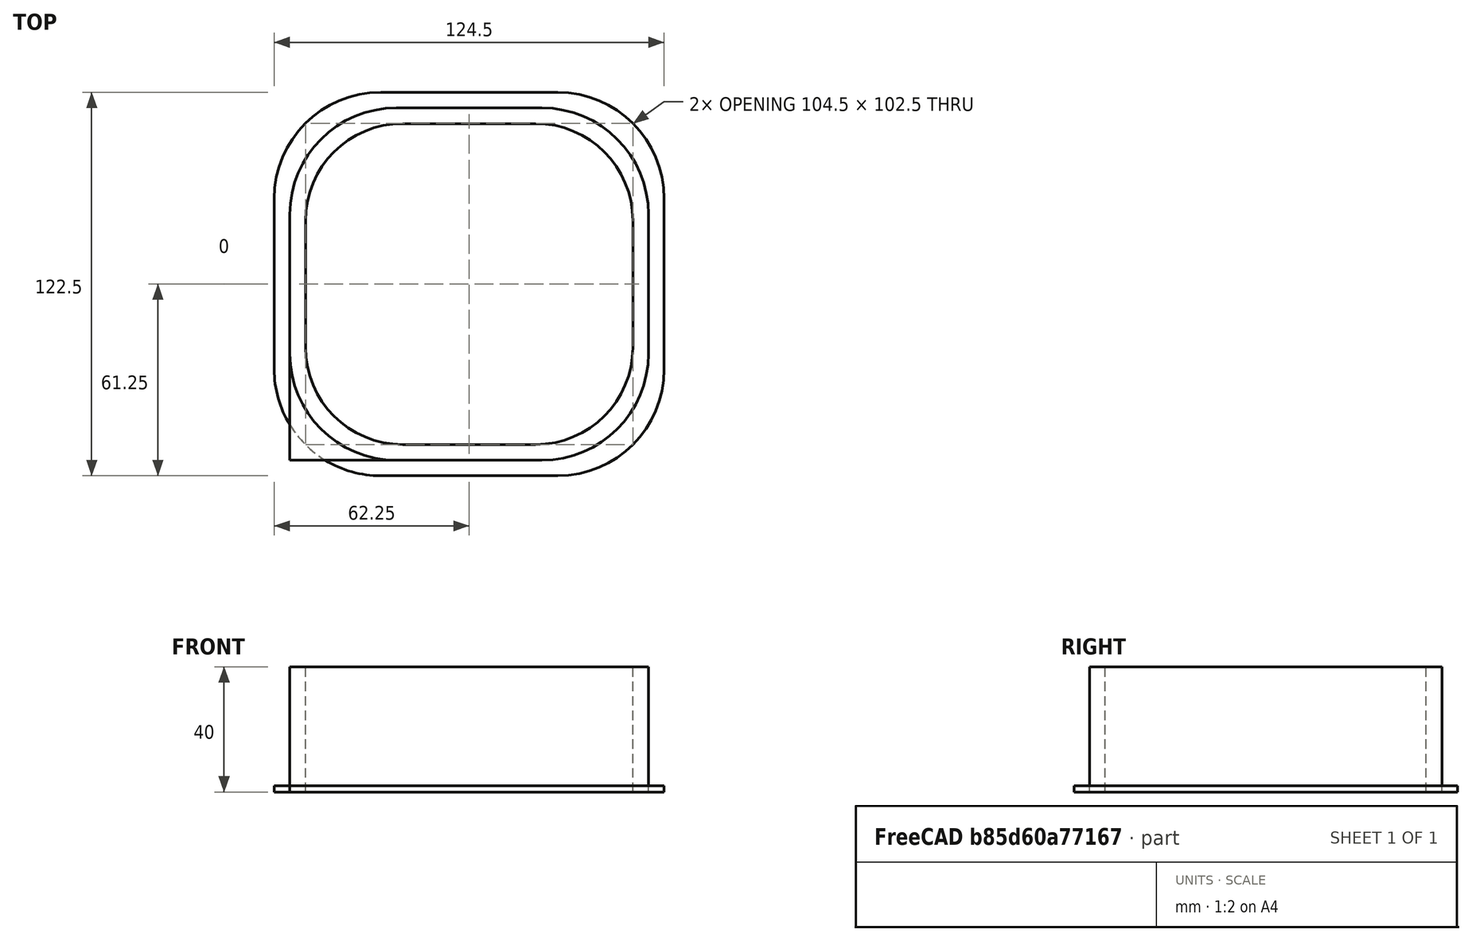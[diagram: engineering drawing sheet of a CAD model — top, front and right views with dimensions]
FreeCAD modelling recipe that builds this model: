
FCSTD DOCUMENT  (FreeCAD 0.14R3703 (Git))
Label: cube_flex
License: CC-BY 3.0
LicenseURL: http://creativecommons.org/licenses/by/3.0/
objects: PartDesign::Fillet×9, Part::Box×2, Part::Fillet×2, Part::Cut×1, Part::MultiFuse×1, App::DocumentObjectGroup×1
note: 15 computed .brp shape members not serialized (recipe doc carries the construction recipe); baked Part::Feature solids carry a one-line shape summary decoded from their .brp

FEATURE [Part::Box] Box  label="Cubo"
  Height = 40
  Length = 114.5
  Width = 112.5
FEATURE [Part::Box] Box001  label="Cubo001"
  Height = 42
  Length = 104.5
  Placement = pos=(5,5,0) rot=(0,0,1;0rad)
  Width = 102.5
FEATURE [Part::Cut] Cut
  Base = -> Box
  Tool = -> Box001
FEATURE [PartDesign::Fillet] Fillet
  Base = -> Cut [Edge24]
  Radius = 31
FEATURE [PartDesign::Fillet] Fillet001
  Base = -> Fillet [Edge11]
  Radius = 31
FEATURE [PartDesign::Fillet] Fillet002
  Base = -> Fillet001 [Edge20]
  Radius = 31
FEATURE [PartDesign::Fillet] Fillet003
  Base = -> Fillet002 [Edge19]
  Radius = 31
FEATURE [PartDesign::Fillet] Fillet004
  Base = -> Fillet003 [Edge30]
  Radius = 34
FEATURE [PartDesign::Fillet] Fillet005
  Base = -> Fillet004 [Edge22]
  Radius = 34
FEATURE [PartDesign::Fillet] Fillet006
  Base = -> Fillet005 [Edge22]
  Radius = 34
FEATURE [PartDesign::Fillet] Fillet009
  Base = -> Fillet005 [Edge22]
  Radius = 34
FEATURE [PartDesign::Fillet] Fillet008
  Base = -> Fillet009 [Edge24]
  Radius = 34
FEATURE [Part::Fillet] Fillet011
  Base = -> Fillet005
  Edges = 1 edges r=34: [Edge22]
FEATURE [Part::Fillet] Fillet010
  Base = -> Fillet011
  Edges = 1 edges r=34: [Edge24]
  Placement = pos=(-5,-5,0) rot=(0,0,1;0rad)
FEATURE [Part::MultiFuse] Fusion
  Shapes = -> [Fillet010,Fillet008]
FEATURE [App::DocumentObjectGroup] Grupo  label="cube_flex"
  Group = -> [Cut,Fillet,Fillet001,Fillet002,Fillet003,Fillet004,Fillet006,Fillet009,Fusion]
